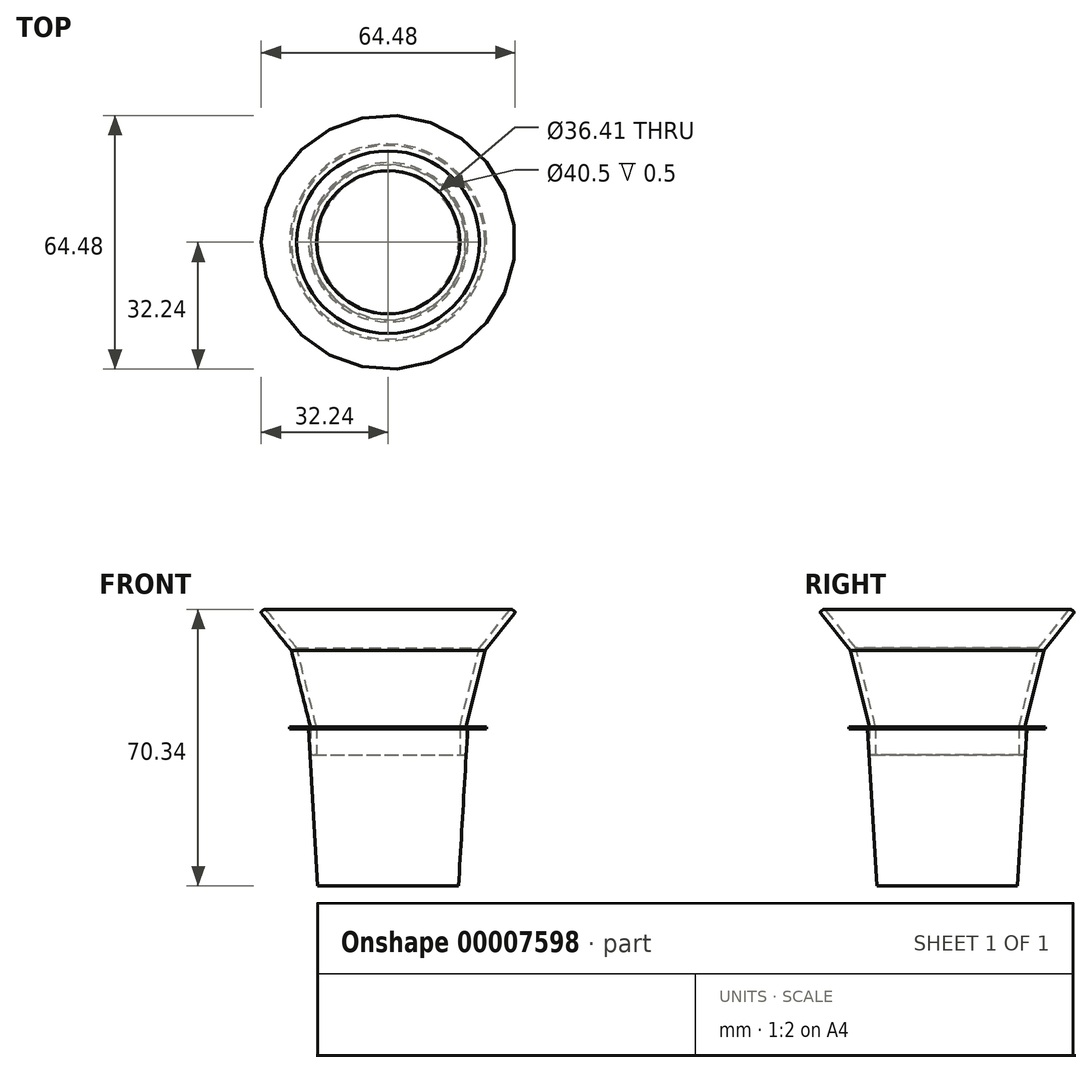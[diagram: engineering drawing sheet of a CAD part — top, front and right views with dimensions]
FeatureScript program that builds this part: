
annotation { "Feature Type Name" : "Feature", "Feature Type Description" : "" }
export const myFeature = defineFeature(function(context is Context, id is Id, definition is map)
    precondition{}
    {
        {
            var Q0;
            Q0=qCreatedBy(makeId("Top.planeOp"),FACE);
            cPlane(context, id + "F0", {"entities" : qUnion([Q0]), "cplaneType" : CPlaneType.OFFSET, "offset" : 40.5 * mm, "width" : 150 * mm, "height" : 150 * mm});
        }
        {
            var Q0;
            Q0=qCreatedBy(id+"F0.planeOp",FACE);
            var sketch = newSketch(context, id + "F1", { "sketchPlane" : qUnion([Q0])});
            skCircle(sketch, "E0", {"center": v(0, 0) * mm, "radius": 25 * mm});
            skCircle(sketch, "E1", {"center": v(0, 0) * mm, "radius": 20.25 * mm});
            skSolve(sketch);
        }
        {
            var Q0;
            Q0=qCreatedBy(makeId("Top.planeOp"),FACE);
            var sketch = newSketch(context, id + "F2", { "sketchPlane" : qUnion([Q0])});
            skCircle(sketch, "E2", {"center": v(0, 0) * mm, "radius": 17.88 * mm});
            skSolve(sketch);
        }
        {
            var Q0;
            Q0=makeQuery(id+"F2.imprint","IMPRINT",FACE,{"disambiguationData":[TD([[makeQuery(id+"F2.imprint","IMPRINT",EDGE,{"derivedFrom":sQuery(id+"F2.wireOp",EDGE,"E2")}),1.0]])]});
            var Q1;
            Q1=makeQuery(id+"F1.imprint","IMPRINT",FACE,{"disambiguationData":[TD([[makeQuery(id+"F1.imprint","IMPRINT",EDGE,{"derivedFrom":sQuery(id+"F1.wireOp",EDGE,"E1")}),1.0]])]});
            loft(context, id + "F3", {"sheetProfilesArray" : [{ "sheetProfileEntities" : qUnion([Q0]) }, { "sheetProfileEntities" : qUnion([Q1]) }]});
        }
        {
            var Q0;
            Q0 = qSketchRegion(id + "F1", true);
            extrude(context, id + "F4", {"entities" : qUnion([Q0]), "operationType" : NewBodyOperationType.ADD, "oppositeDirection" : true, "depth" : 0.5 * mm});
        }
        {
            var Q0;
            Q0=qCreatedBy(makeId("Front.planeOp"),FACE);
            var sketch = newSketch(context, id + "F5", { "sketchPlane" : qUnion([Q0])});
            skLineSegment(sketch, "E3", {"start": v(18.2, 40.5) * mm, "end": v(23.2, 60.5) * mm});
            skLineSegment(sketch, "E4", {"start": v(23.2, 60.5) * mm, "end": v(31.2, 70.5) * mm});
            skLineSegment(sketch, "E5.0", {"start": v(24.58, 59.82) * mm, "end": v(32.43, 69.63) * mm});
            skLineSegment(sketch, "E5.1", {"start": v(19.75, 40.5) * mm, "end": v(24.58, 59.82) * mm});
            skLineSegment(sketch, "E6", {"start": v(31.2, 70.5) * mm, "end": v(32.43, 69.63) * mm});
            skLineSegment(sketch, "E7", {"start": v(18.2, 40.5) * mm, "end": v(19.75, 40.5) * mm});
            skLineSegment(sketch, "E8", {"start": v(0, 0) * mm, "end": v(0, 71.44) * mm, "construction": true});
            skLineSegment(sketch, "E9", {"start": v(26.04, 0) * mm, "end": v(24.58, 59.82) * mm, "construction": true});
            skLineSegment(sketch, "E10", {"start": v(18.2, 40.5) * mm, "end": v(18.2, 33.32) * mm});
            skLineSegment(sketch, "E11", {"start": v(18.2, 33.32) * mm, "end": v(19.75, 33.32) * mm});
            skLineSegment(sketch, "E12", {"start": v(19.75, 33.32) * mm, "end": v(19.75, 40.5) * mm});
            skSolve(sketch);
        }
        {
            var Q0;
            Q0=makeQuery(id+"F5.imprint","IMPRINT",FACE,{"disambiguationData":[TD([[makeQuery(id+"F5.imprint","IMPRINT",EDGE,{"derivedFrom":sQuery(id+"F5.wireOp",EDGE,"E3")}),-1.0]])]});
            var Q1;
            Q1=makeQuery(id+"F5.imprint","IMPRINT",FACE,{"disambiguationData":[TD([[makeQuery(id+"F5.imprint","IMPRINT",EDGE,{"derivedFrom":sQuery(id+"F5.wireOp",EDGE,"E7")}),-1.0]])]});
            var Q2;
            Q2=sQuery(id+"F5.wireOp",EDGE,"E8");
            revolve(context, id + "F6", {"entities" : qUnion([Q0, Q1]), "axis" : qUnion([Q2]), "revolveType" : RevolveType.FULL});
        }
        {
            var Q0;
            Q0=makeQuery(id+"F6.opRevolve","SWEPT_EDGE",EDGE,{"disambiguationData":[OSD([sQuery(id+"F5.wireOp",EDGE,"E11"),sQuery(id+"F5.wireOp",EDGE,"E12")])]});
            var Q1;
            Q1=makeQuery(id+"F6.opRevolve","SWEPT_EDGE",EDGE,{"disambiguationData":[OSD([sQuery(id+"F5.wireOp",EDGE,"E10"),sQuery(id+"F5.wireOp",EDGE,"E11")])]});
            fillet(context, id + "F7", {"entities" : qUnion([Q0, Q1]), "radius" : 0.5 * mm, "tangentPropagation" : true, "rho" : 0.5, "crossSection" : FilletCrossSection.CONIC, "allowEdgeOverflow" : false});
        }
        {
            var Q0;
            Q0=makeQuery(id+"F6.opRevolve","SWEPT_FACE",FACE,{"disambiguationData":[OSD([sQuery(id+"F5.wireOp",EDGE,"E6")])]});
            fillet(context, id + "F8", {"entities" : qUnion([Q0]), "radius" : 0.5 * mm, "tangentPropagation" : true, "rho" : 0.5, "crossSection" : FilletCrossSection.CONIC, "allowEdgeOverflow" : false});
        }
    });
